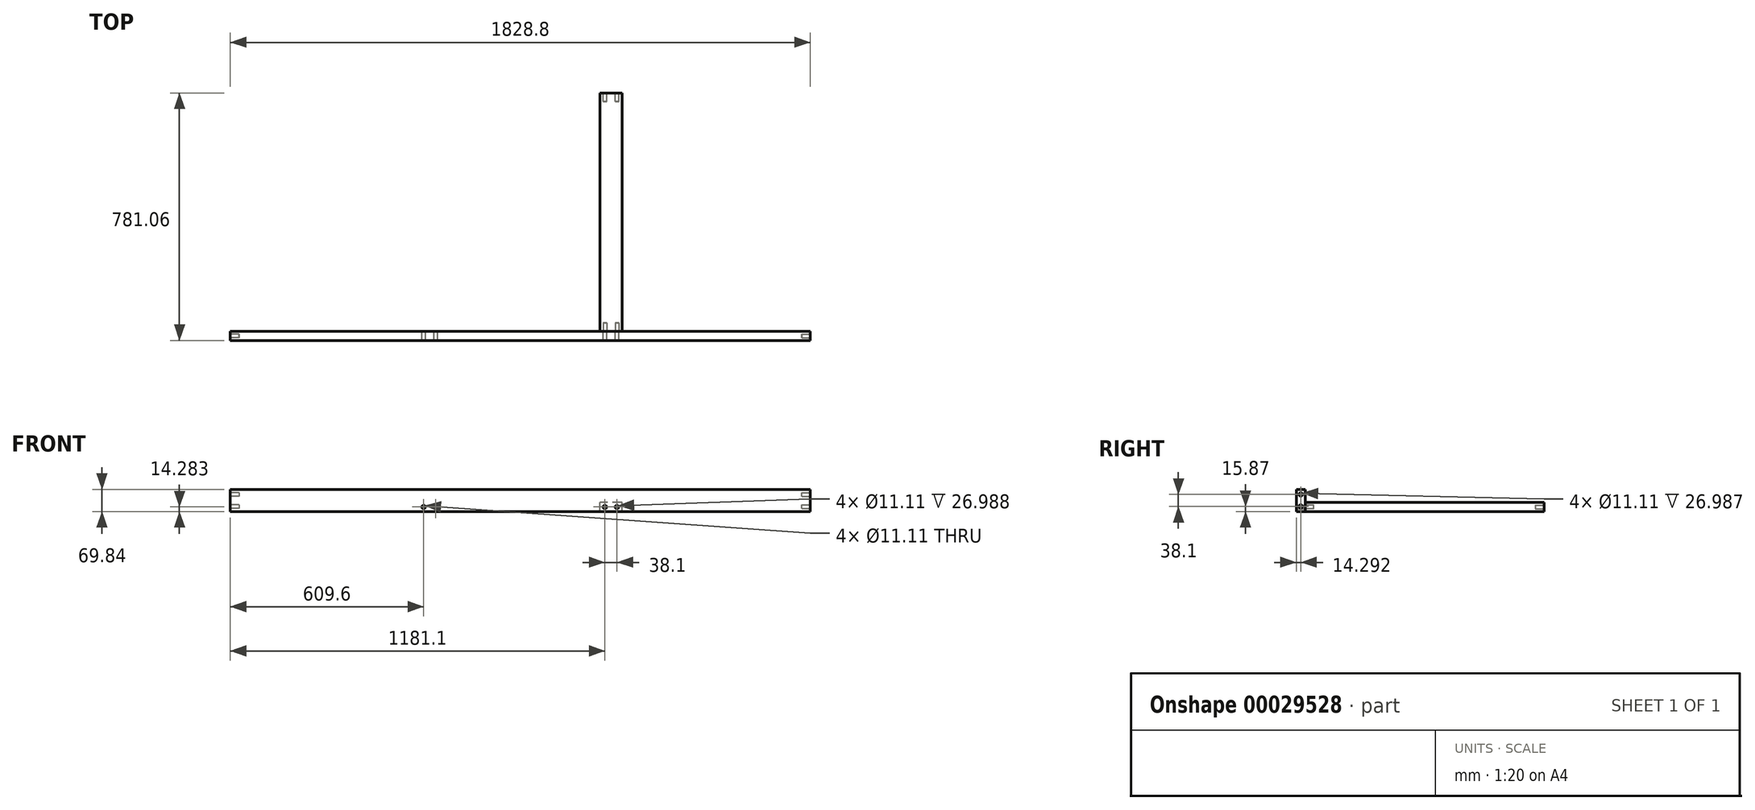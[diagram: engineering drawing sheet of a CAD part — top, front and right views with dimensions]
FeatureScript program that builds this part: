
annotation { "Feature Type Name" : "Feature", "Feature Type Description" : "" }
export const myFeature = defineFeature(function(context is Context, id is Id, definition is map)
    precondition{}
    {
        {
            var Q0;
            Q0=qCreatedBy(makeId("Front.planeOp"),FACE);
            var sketch = newSketch(context, id + "F0", { "sketchPlane" : qUnion([Q0])});
            skLineSegment(sketch, "E0.rect.bottom", {"start": v(914.4, 34.93) * mm, "end": v(-914.4, 34.93) * mm});
            skLineSegment(sketch, "E0.rect.top", {"start": v(914.4, -34.93) * mm, "end": v(-914.4, -34.93) * mm});
            skLineSegment(sketch, "E0.rect.left", {"start": v(914.4, 34.93) * mm, "end": v(914.4, -34.93) * mm});
            skLineSegment(sketch, "E0.rect.right", {"start": v(-914.4, 34.93) * mm, "end": v(-914.4, -34.93) * mm});
            skPoint(sketch, "E0.rect.middle", {"position": v(0, 0) * mm});
            skCircle(sketch, "E1", {"center": v(266.7, -20.64) * mm, "radius": 5.56 * mm});
            skCircle(sketch, "E2", {"center": v(304.8, -20.64) * mm, "radius": 5.56 * mm});
            skLineSegment(sketch, "E3", {"start": v(0, 34.93) * mm, "end": v(0, -34.93) * mm, "construction": true});
            skCircle(sketch, "E4.MirrorC", {"center": v(-266.7, -20.64) * mm, "radius": 5.56 * mm});
            skCircle(sketch, "E5.MirrorC", {"center": v(-304.8, -20.64) * mm, "radius": 5.56 * mm});
            skSolve(sketch);
        }
        {
            var Q0;
            Q0=makeQuery(id+"F0.imprint","IMPRINT",FACE,{"disambiguationData":[TD([[makeQuery(id+"F0.imprint","IMPRINT",EDGE,{"derivedFrom":sQuery(id+"F0.wireOp",EDGE,"E0.rect.bottom")}),1.0]])]});
            extrude(context, id + "F1", {"entities" : qUnion([Q0]), "depth" : 28.57 * mm});
        }
        {
            var Q0;
            Q0=makeQuery(id+"F1.opExtrude","SWEPT_FACE",FACE,{"disambiguationData":[OSD([sQuery(id+"F0.wireOp",EDGE,"E0.rect.left")])]});
            var sketch = newSketch(context, id + "F2", { "sketchPlane" : qUnion([Q0])});
            skCircle(sketch, "E6", {"center": v(-14.29, 19.05) * mm, "radius": 5.56 * mm});
            skCircle(sketch, "E7", {"center": v(-14.29, -19.05) * mm, "radius": 5.56 * mm});
            skSolve(sketch);
        }
        {
            var Q0;
            Q0=makeQuery(id+"F2.imprint","IMPRINT",FACE,{"disambiguationData":[TD([[makeQuery(id+"F2.imprint","IMPRINT",EDGE,{"derivedFrom":sQuery(id+"F2.wireOp",EDGE,"E7")}),1.0]])]});
            var Q1;
            Q1=makeQuery(id+"F2.imprint","IMPRINT",FACE,{"disambiguationData":[TD([[makeQuery(id+"F2.imprint","IMPRINT",EDGE,{"derivedFrom":sQuery(id+"F2.wireOp",EDGE,"E6")}),1.0]])]});
            extrude(context, id + "F3", {"entities" : qUnion([Q0, Q1]), "operationType" : NewBodyOperationType.REMOVE, "oppositeDirection" : true, "depth" : 26.99 * mm});
        }
        {
            var Q0;
            Q0=makeQuery(id+"F1.opExtrude","SWEPT_FACE",FACE,{"disambiguationData":[OSD([sQuery(id+"F0.wireOp",EDGE,"E0.rect.right")])]});
            var sketch = newSketch(context, id + "F4", { "sketchPlane" : qUnion([Q0])});
            skLineSegment(sketch, "E8", {"start": v(14.29, 34.92) * mm, "end": v(14.29, -34.93) * mm, "construction": true});
            skPoint(sketch, "E9", {"position": v(14.29, 19.05) * mm});
            skPoint(sketch, "E10", {"position": v(14.29, -19.05) * mm});
            skCircle(sketch, "E11", {"center": v(14.29, 19.05) * mm, "radius": 5.56 * mm});
            skCircle(sketch, "E12", {"center": v(14.29, -19.05) * mm, "radius": 5.56 * mm});
            skSolve(sketch);
        }
        {
            var Q0;
            Q0 = qSketchRegion(id + "F4", true);
            extrude(context, id + "F5", {"entities" : qUnion([Q0]), "operationType" : NewBodyOperationType.REMOVE, "oppositeDirection" : true, "depth" : 26.99 * mm});
        }
        {
            var Q0;
            Q0=makeQuery(id+"F1.opExtrude","CAP_FACE",FACE,{"disambiguationData":[OSD([sQuery(id+"F0.wireOp",EDGE,"E0.rect.bottom"),sQuery(id+"F0.wireOp",EDGE,"E0.rect.top"),sQuery(id+"F0.wireOp",EDGE,"E0.rect.left"),sQuery(id+"F0.wireOp",EDGE,"E0.rect.right"),sQuery(id+"F0.wireOp",EDGE,"E1"),sQuery(id+"F0.wireOp",EDGE,"E2"),sQuery(id+"F0.wireOp",EDGE,"E4.MirrorC"),sQuery(id+"F0.wireOp",EDGE,"E5.MirrorC")])],"isStart":true});
            var sketch = newSketch(context, id + "F6", { "sketchPlane" : qUnion([Q0])});
            skLineSegment(sketch, "E13.bottom", {"start": v(-320.67, -34.93) * mm, "end": v(-250.82, -34.93) * mm});
            skLineSegment(sketch, "E13.top", {"start": v(-320.67, -6.35) * mm, "end": v(-250.82, -6.35) * mm});
            skLineSegment(sketch, "E13.left", {"start": v(-320.67, -34.93) * mm, "end": v(-320.67, -6.35) * mm});
            skLineSegment(sketch, "E13.right", {"start": v(-250.82, -34.92) * mm, "end": v(-250.82, -6.35) * mm});
            skPoint(sketch, "E14", {"position": v(-304.8, -20.64) * mm});
            skPoint(sketch, "E15", {"position": v(-266.7, -20.64) * mm});
            skLineSegment(sketch, "E16", {"start": v(-304.8, -20.64) * mm, "end": v(-266.7, -20.64) * mm, "construction": true});
            skPoint(sketch, "E17", {"position": v(-285.75, -20.64) * mm});
            skPoint(sketch, "E18", {"position": v(-285.75, -6.35) * mm});
            skSolve(sketch);
        }
        {
            var Q0;
            Q0=makeQuery(id+"F6.imprint","IMPRINT",FACE,{"disambiguationData":[TD([[makeQuery(id+"F6.imprint","IMPRINT",EDGE,{"derivedFrom":sQuery(id+"F6.wireOp",EDGE,"E13.bottom")}),1.0]])]});
            var Q1;
            Q1=makeQuery(id+"F6.imprint","IMPRINT",FACE,{"disambiguationData":[TD([[makeQuery(id+"F6.imprint","IMPRINT",EDGE,{"derivedFrom":makeQuery(id+"F1.opExtrude","CAP_EDGE",EDGE,{"disambiguationData":[OSD([sQuery(id+"F0.wireOp",EDGE,"E2")])],"isStart":true})}),-1.0]])]});
            var Q2;
            Q2=makeQuery(id+"F6.imprint","IMPRINT",FACE,{"disambiguationData":[TD([[makeQuery(id+"F6.imprint","IMPRINT",EDGE,{"derivedFrom":makeQuery(id+"F1.opExtrude","CAP_EDGE",EDGE,{"disambiguationData":[OSD([sQuery(id+"F0.wireOp",EDGE,"E1")])],"isStart":true})}),-1.0]])]});
            extrude(context, id + "F7", {"entities" : qUnion([Q0, Q1, Q2]), "depth" : 752.47 * mm});
        }
        {
            var Q0;
            Q0=makeQuery(id+"F7.opExtrude","CAP_FACE",FACE,{"disambiguationData":[OSD([sQuery(id+"F6.wireOp",EDGE,"E13.bottom"),sQuery(id+"F6.wireOp",EDGE,"E13.top"),sQuery(id+"F6.wireOp",EDGE,"E13.left"),sQuery(id+"F6.wireOp",EDGE,"E13.right")])],"isStart":true});
            var sketch = newSketch(context, id + "F8", { "sketchPlane" : qUnion([Q0])});
            skCircle(sketch, "E19.0", {"center": v(266.7, -20.64) * mm, "radius": 5.56 * mm});
            skCircle(sketch, "E20.0", {"center": v(304.8, -20.64) * mm, "radius": 5.56 * mm});
            skSolve(sketch);
        }
        {
            var Q0;
            Q0 = qSketchRegion(id + "F8", true);
            extrude(context, id + "F9", {"entities" : qUnion([Q0]), "operationType" : NewBodyOperationType.REMOVE, "oppositeDirection" : true, "depth" : 26.99 * mm});
        }
        {
            var Q0;
            Q0=makeQuery(id+"F7.opExtrude","CAP_FACE",FACE,{"disambiguationData":[OSD([sQuery(id+"F6.wireOp",EDGE,"E13.bottom"),sQuery(id+"F6.wireOp",EDGE,"E13.top"),sQuery(id+"F6.wireOp",EDGE,"E13.left"),sQuery(id+"F6.wireOp",EDGE,"E13.right")])],"isStart":false});
            var sketch = newSketch(context, id + "F10", { "sketchPlane" : qUnion([Q0])});
            skCircle(sketch, "E21.0", {"center": v(-304.8, -20.64) * mm, "radius": 5.56 * mm});
            skCircle(sketch, "E22.0", {"center": v(-266.7, -20.64) * mm, "radius": 5.56 * mm});
            skSolve(sketch);
        }
        {
            var Q0;
            Q0 = qSketchRegion(id + "F10", true);
            extrude(context, id + "F11", {"entities" : qUnion([Q0]), "operationType" : NewBodyOperationType.REMOVE, "oppositeDirection" : true, "depth" : 26.99 * mm});
        }
    });
